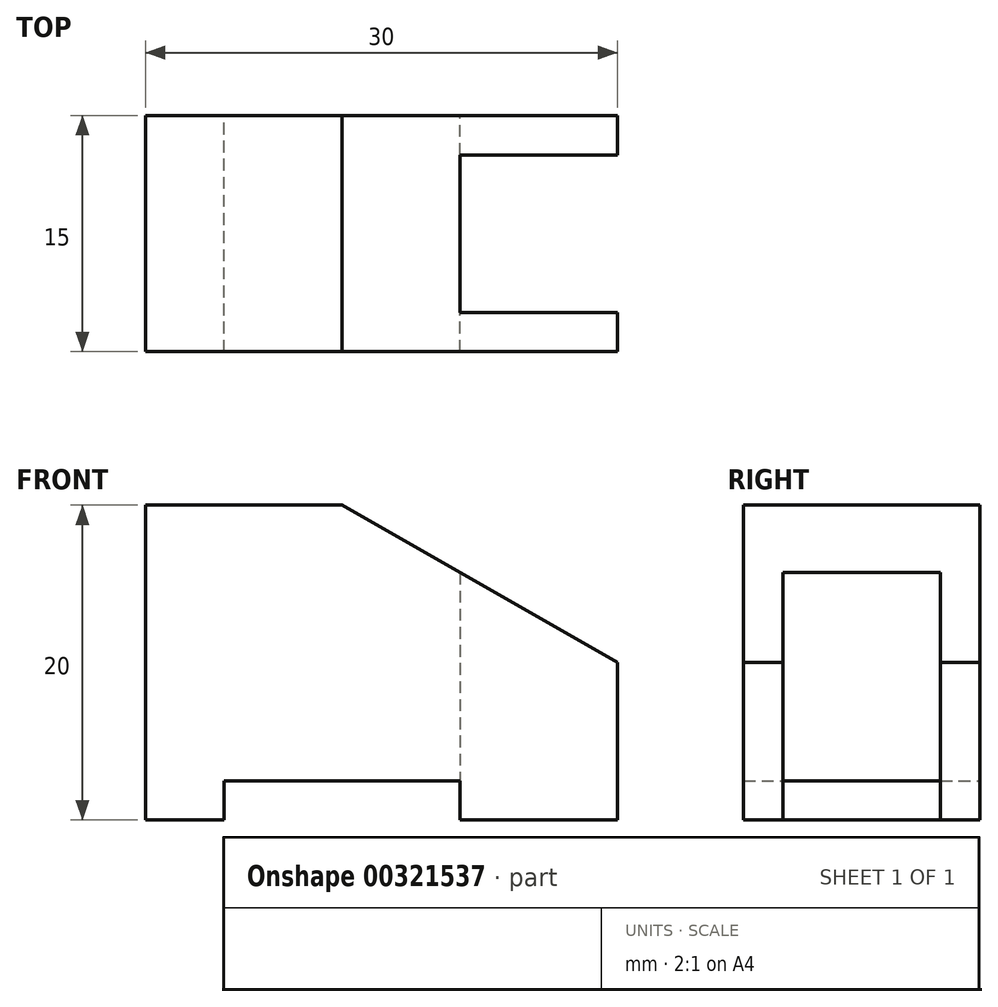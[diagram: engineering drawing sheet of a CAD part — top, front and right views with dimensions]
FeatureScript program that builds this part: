
annotation { "Feature Type Name" : "Feature", "Feature Type Description" : "" }
export const myFeature = defineFeature(function(context is Context, id is Id, definition is map)
    precondition{}
    {
        {
            var Q0;
            Q0=qCreatedBy(makeId("Front.planeOp"),FACE);
            var sketch = newSketch(context, id + "F0", { "sketchPlane" : qUnion([Q0])});
            skLineSegment(sketch, "E0", {"start": v(0, 0) * mm, "end": v(0, 20) * mm});
            skLineSegment(sketch, "E1", {"start": v(0, 20) * mm, "end": v(12.5, 20) * mm});
            skLineSegment(sketch, "E2", {"start": v(12.5, 20) * mm, "end": v(30, 10) * mm});
            skLineSegment(sketch, "E3", {"start": v(30, 10) * mm, "end": v(30, 0) * mm});
            skLineSegment(sketch, "E4", {"start": v(0, 0) * mm, "end": v(5, 0) * mm});
            skLineSegment(sketch, "E5", {"start": v(5, 0) * mm, "end": v(5, 2.5) * mm});
            skLineSegment(sketch, "E6", {"start": v(5, 2.5) * mm, "end": v(20, 2.5) * mm});
            skLineSegment(sketch, "E7", {"start": v(20, 2.5) * mm, "end": v(20, 0) * mm});
            skLineSegment(sketch, "E8", {"start": v(20, 0) * mm, "end": v(30, 0) * mm});
            skSolve(sketch);
        }
        {
            var Q0;
            Q0=makeQuery(id+"F0.imprint","IMPRINT",FACE,{"disambiguationData":[TD([[makeQuery(id+"F0.imprint","IMPRINT",EDGE,{"derivedFrom":sQuery(id+"F0.wireOp",EDGE,"E0")}),-1.0]])]});
            extrude(context, id + "F1", {"entities" : qUnion([Q0]), "depth" : 15 * mm});
        }
        {
            var Q0;
            Q0=makeQuery(id+"F1.opExtrude","SWEPT_FACE",FACE,{"disambiguationData":[OSD([sQuery(id+"F0.wireOp",EDGE,"E8")])]});
            var sketch = newSketch(context, id + "F2", { "sketchPlane" : qUnion([Q0])});
            skLineSegment(sketch, "E9", {"start": v(30, 12.5) * mm, "end": v(20, 12.5) * mm});
            skLineSegment(sketch, "E10", {"start": v(20, 12.5) * mm, "end": v(20, 2.5) * mm});
            skLineSegment(sketch, "E11", {"start": v(20, 2.5) * mm, "end": v(30, 2.5) * mm});
            skLineSegment(sketch, "E12", {"start": v(30, 2.5) * mm, "end": v(30, 12.5) * mm});
            skSolve(sketch);
        }
        {
            var Q0;
            Q0=makeQuery(id+"F2.imprint","IMPRINT",FACE,{"disambiguationData":[TD([[makeQuery(id+"F2.imprint","IMPRINT",EDGE,{"derivedFrom":sQuery(id+"F2.wireOp",EDGE,"E9")}),1.0]])]});
            extrude(context, id + "F3", {"entities" : qUnion([Q0]), "operationType" : NewBodyOperationType.REMOVE, "endBound" : BoundingType.THROUGH_ALL, "oppositeDirection" : true, "depth" : 25 * mm});
        }
    });
